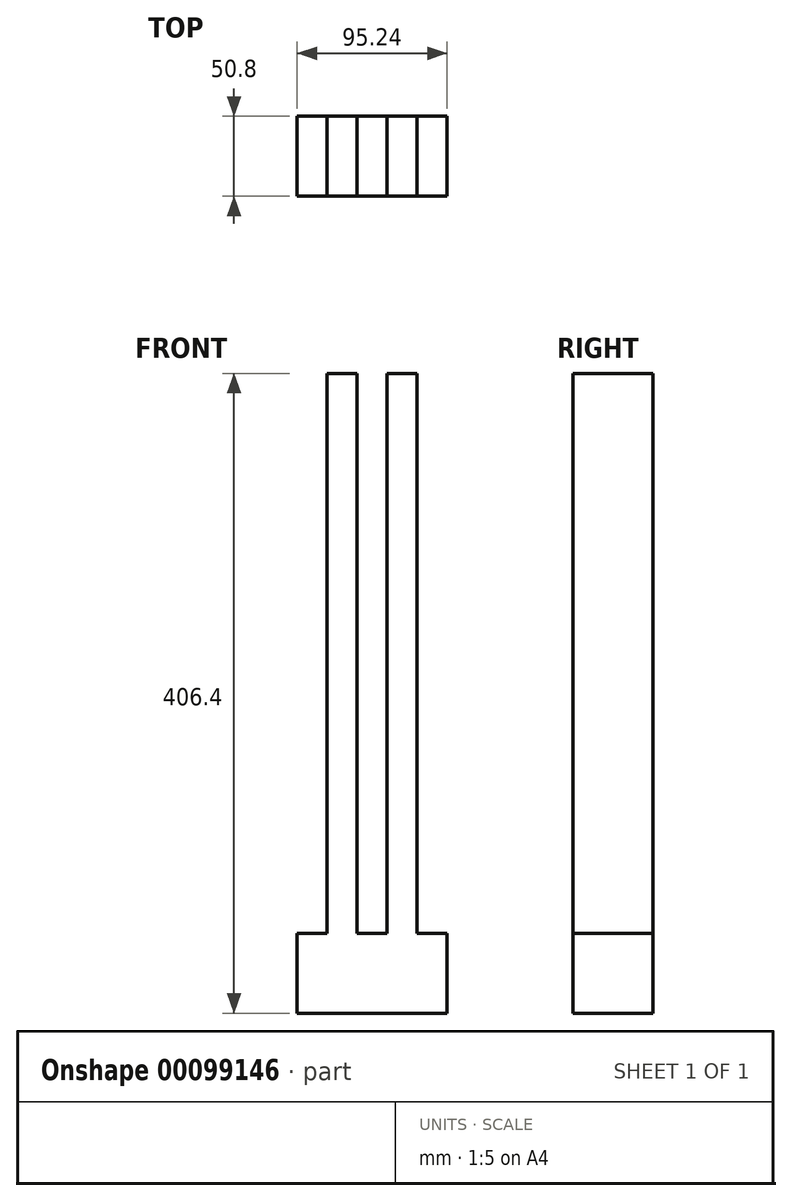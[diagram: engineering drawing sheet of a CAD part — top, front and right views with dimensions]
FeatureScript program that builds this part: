
annotation { "Feature Type Name" : "Feature", "Feature Type Description" : "" }
export const myFeature = defineFeature(function(context is Context, id is Id, definition is map)
    precondition{}
    {
        {
            var Q0;
            Q0=qCreatedBy(makeId("Top.planeOp"),FACE);
            var sketch = newSketch(context, id + "F0", { "sketchPlane" : qUnion([Q0])});
            skLineSegment(sketch, "E0.bottom", {"start": v(-47.62, 25.4) * mm, "end": v(-28.57, 25.4) * mm});
            skLineSegment(sketch, "E0.top", {"start": v(-47.62, -25.4) * mm, "end": v(-28.57, -25.4) * mm});
            skLineSegment(sketch, "E0.left", {"start": v(-47.62, 25.4) * mm, "end": v(-47.62, -25.4) * mm});
            skLineSegment(sketch, "E0.right", {"start": v(-28.57, 25.4) * mm, "end": v(-28.57, -25.4) * mm});
            skPoint(sketch, "E1", {"position": v(-28.57, 0) * mm});
            skPoint(sketch, "E2", {"position": v(-47.62, 0) * mm});
            skLineSegment(sketch, "E3.bottom", {"start": v(-28.57, 25.4) * mm, "end": v(-9.53, 25.4) * mm});
            skLineSegment(sketch, "E3.top", {"start": v(-28.57, -25.4) * mm, "end": v(-9.53, -25.4) * mm});
            skLineSegment(sketch, "E3.right", {"start": v(-9.53, 25.4) * mm, "end": v(-9.53, -25.4) * mm});
            skPoint(sketch, "E4", {"position": v(-9.52, 0) * mm});
            skLineSegment(sketch, "E5.bottom", {"start": v(-9.53, 25.4) * mm, "end": v(9.53, 25.4) * mm});
            skLineSegment(sketch, "E5.top", {"start": v(-9.53, -25.4) * mm, "end": v(9.53, -25.4) * mm});
            skLineSegment(sketch, "E5.left", {"start": v(-9.53, 25.4) * mm, "end": v(-9.52, -25.4) * mm});
            skLineSegment(sketch, "E5.right", {"start": v(9.52, 25.4) * mm, "end": v(9.53, -25.4) * mm});
            skPoint(sketch, "E6", {"position": v(9.52, 0) * mm});
            skLineSegment(sketch, "E7.bottom", {"start": v(9.53, 25.4) * mm, "end": v(28.58, 25.4) * mm});
            skLineSegment(sketch, "E7.top", {"start": v(9.53, -25.4) * mm, "end": v(28.58, -25.4) * mm});
            skLineSegment(sketch, "E7.right", {"start": v(28.57, 25.4) * mm, "end": v(28.58, -25.4) * mm});
            skPoint(sketch, "E8", {"position": v(28.58, 0) * mm});
            skLineSegment(sketch, "E9.bottom", {"start": v(28.58, 25.4) * mm, "end": v(47.63, 25.4) * mm});
            skLineSegment(sketch, "E9.top", {"start": v(28.58, -25.4) * mm, "end": v(47.63, -25.4) * mm});
            skLineSegment(sketch, "E9.left", {"start": v(28.58, 25.4) * mm, "end": v(28.57, -25.4) * mm});
            skLineSegment(sketch, "E9.right", {"start": v(47.63, 25.4) * mm, "end": v(47.63, -25.4) * mm});
            skPoint(sketch, "E10", {"position": v(47.63, 0) * mm});
            skLineSegment(sketch, "E11", {"start": v(-9.52, 0) * mm, "end": v(9.52, 0) * mm, "construction": true});
            skPoint(sketch, "E12", {"position": v(0, 0) * mm});
            skPoint(sketch, "E12.positionSnap0", {"position": v(0, 0) * mm});
            skSolve(sketch);
        }
        {
            var Q0;
            Q0=makeQuery(id+"F0.imprint","IMPRINT",FACE,{"disambiguationData":[TD([[makeQuery(id+"F0.imprint","IMPRINT",EDGE,{"derivedFrom":sQuery(id+"F0.wireOp",EDGE,"E0.bottom")}),-1.0]])]});
            var Q1;
            Q1=makeQuery(id+"F0.imprint","IMPRINT",FACE,{"disambiguationData":[TD([[makeQuery(id+"F0.imprint","IMPRINT",EDGE,{"derivedFrom":sQuery(id+"F0.wireOp",EDGE,"E5.bottom")}),-1.0]])]});
            var Q2;
            Q2=makeQuery(id+"F0.imprint","IMPRINT",FACE,{"disambiguationData":[TD([[makeQuery(id+"F0.imprint","IMPRINT",EDGE,{"derivedFrom":sQuery(id+"F0.wireOp",EDGE,"E7.bottom")}),-1.0]])]});
            var Q3;
            Q3=makeQuery(id+"F0.imprint","IMPRINT",FACE,{"disambiguationData":[TD([[makeQuery(id+"F0.imprint","IMPRINT",EDGE,{"derivedFrom":sQuery(id+"F0.wireOp",EDGE,"E9.bottom")}),-1.0]])]});
            var Q4;
            Q4=makeQuery(id+"F0.imprint","IMPRINT",FACE,{"disambiguationData":[TD([[makeQuery(id+"F0.imprint","IMPRINT",EDGE,{"derivedFrom":sQuery(id+"F0.wireOp",EDGE,"E3.bottom")}),-1.0]])]});
            extrude(context, id + "F1", {"entities" : qUnion([Q0, Q1, Q2, Q3, Q4]), "depth" : 50.8 * mm});
        }
        {
            var Q0;
            Q0=makeQuery(id+"F0.imprint","IMPRINT",FACE,{"disambiguationData":[TD([[makeQuery(id+"F0.imprint","IMPRINT",EDGE,{"derivedFrom":sQuery(id+"F0.wireOp",EDGE,"E7.bottom")}),-1.0]])]});
            var Q1;
            Q1=makeQuery(id+"F0.imprint","IMPRINT",FACE,{"disambiguationData":[TD([[makeQuery(id+"F0.imprint","IMPRINT",EDGE,{"derivedFrom":sQuery(id+"F0.wireOp",EDGE,"E3.bottom")}),-1.0]])]});
            extrude(context, id + "F2", {"entities" : qUnion([Q0, Q1]), "operationType" : NewBodyOperationType.ADD, "depth" : 406.4 * mm});
        }
    });
